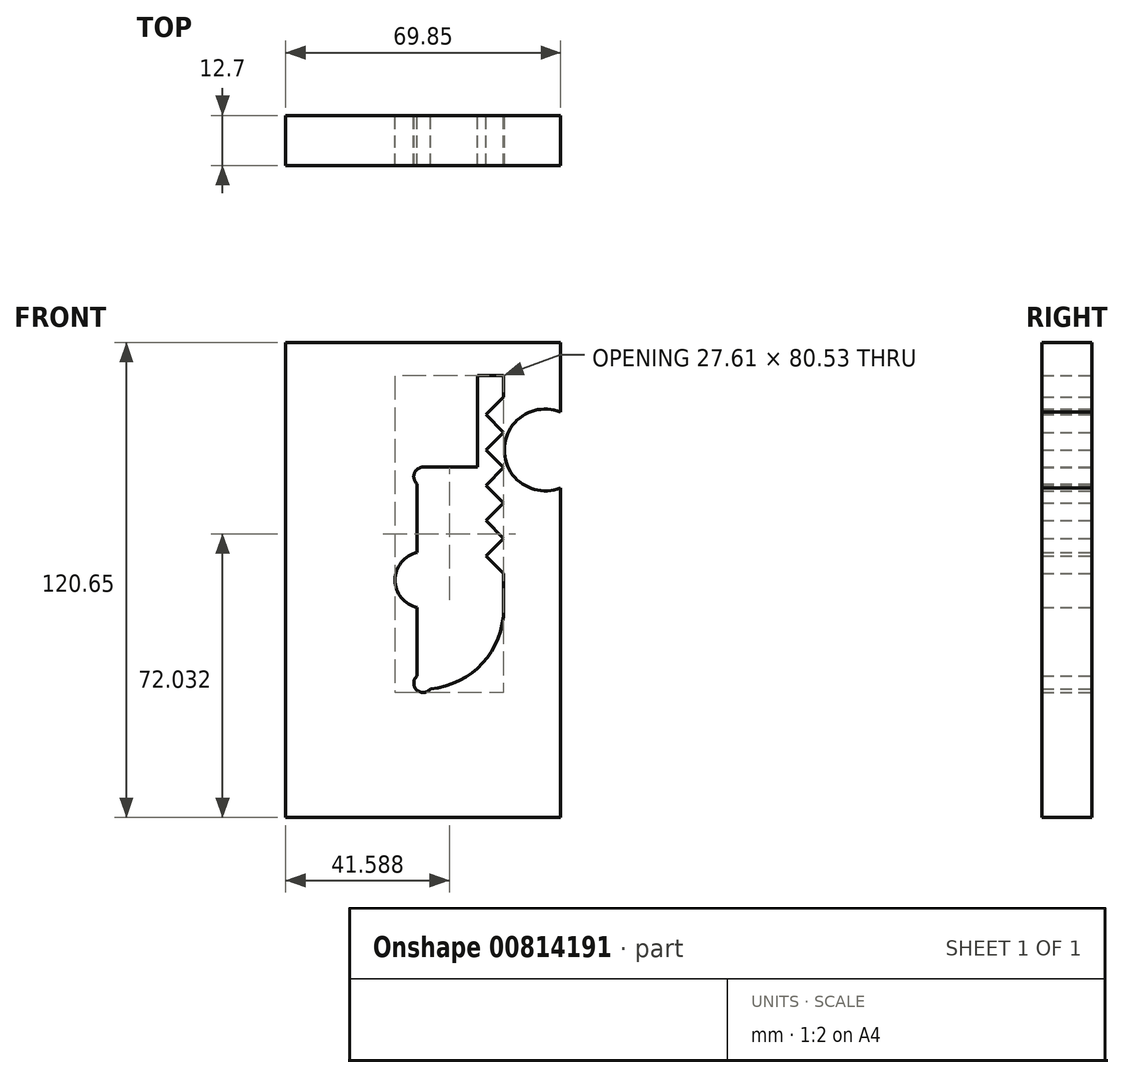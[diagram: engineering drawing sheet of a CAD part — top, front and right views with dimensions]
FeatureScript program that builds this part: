
annotation { "Feature Type Name" : "Feature", "Feature Type Description" : "" }
export const myFeature = defineFeature(function(context is Context, id is Id, definition is map)
    precondition{}
    {
        {
            var Q0;
            Q0=qCreatedBy(makeId("Front.planeOp"),FACE);
            var sketch = newSketch(context, id + "F0", { "sketchPlane" : qUnion([Q0])});
            skLineSegment(sketch, "E0.bottom", {"start": v(-44.77, 47.96) * mm, "end": v(25.08, 47.96) * mm});
            skLineSegment(sketch, "E0.top", {"start": v(-44.77, -72.7) * mm, "end": v(25.08, -72.7) * mm});
            skLineSegment(sketch, "E0.left", {"start": v(-44.77, 47.96) * mm, "end": v(-44.77, -72.7) * mm});
            skLineSegment(sketch, "E0.right", {"start": v(25.08, 47.96) * mm, "end": v(25.08, -72.7) * mm});
            skPoint(sketch, "E0.middle", {"position": v(-9.84, -12.37) * mm});
            skCircle(sketch, "E1", {"center": v(-9.84, -12.37) * mm, "radius": 5.56 * mm});
            skCircle(sketch, "E2", {"center": v(-9.84, -12.37) * mm, "radius": 7.14 * mm});
            skCircle(sketch, "E3", {"center": v(-9.84, -38.55) * mm, "radius": 2.38 * mm});
            skLineSegment(sketch, "E4", {"start": v(-11.36, -19.35) * mm, "end": v(-11.36, -36.7) * mm});
            skLineSegment(sketch, "E5", {"start": v(-8.27, -19.33) * mm, "end": v(-8.27, -36.76) * mm});
            skLineSegment(sketch, "E6", {"start": v(-11.36, -5.38) * mm, "end": v(-11.36, 12.08) * mm});
            skLineSegment(sketch, "E7", {"start": v(-8.33, -5.38) * mm, "end": v(-8.33, 12.1) * mm});
            skCircle(sketch, "E8", {"center": v(-9.86, 13.93) * mm, "radius": 2.38 * mm});
            skPoint(sketch, "E8.third.point", {"position": v(-9.84, 16.31) * mm});
            skLineSegment(sketch, "E9", {"start": v(-9.84, 16.31) * mm, "end": v(3.94, 16.31) * mm});
            skLineSegment(sketch, "E10", {"start": v(3.94, 16.31) * mm, "end": v(3.94, 12.1) * mm});
            skLineSegment(sketch, "E11", {"start": v(3.94, 12.1) * mm, "end": v(-8.33, 12.1) * mm});
            skLineSegment(sketch, "E12", {"start": v(3.94, -19.73) * mm, "end": v(3.94, 16.31) * mm});
            skLineSegment(sketch, "E13", {"start": v(3.94, -19.73) * mm, "end": v(3.94, -19.73) * mm});
            skLineSegment(sketch, "E14", {"start": v(10.62, -19.73) * mm, "end": v(3.94, -19.73) * mm});
            skLineSegment(sketch, "E15", {"start": v(3.94, 16.31) * mm, "end": v(3.94, 39.6) * mm});
            skLineSegment(sketch, "E16", {"start": v(3.94, 39.6) * mm, "end": v(10.62, 39.6) * mm});
            skLineSegment(sketch, "E17", {"start": v(10.62, 39.6) * mm, "end": v(10.62, 34.15) * mm});
            skPoint(sketch, "E18.endSnap0", {"position": v(3.94, -1.7) * mm});
            skArc(sketch, "E19", {"start": v(-7.95, -40) * mm, "mid": v(5.28, -33.48) * mm, "end": v(10.62, -19.73) * mm});
            skArc(sketch, "E20", {"start": v(-8.27, -36.76) * mm, "mid": v(0.57, -30.2) * mm, "end": v(3.94, -19.73) * mm});
            skLineSegment(sketch, "E21", {"start": v(10.62, 34.15) * mm, "end": v(6.13, 29.66) * mm});
            skLineSegment(sketch, "E22", {"start": v(6.13, 29.66) * mm, "end": v(10.62, 25.17) * mm});
            skLineSegment(sketch, "E23", {"start": v(10.62, 25.17) * mm, "end": v(6.14, 20.68) * mm});
            skLineSegment(sketch, "E24", {"start": v(6.14, 20.68) * mm, "end": v(10.62, 16.2) * mm});
            skLineSegment(sketch, "E25", {"start": v(10.62, 16.2) * mm, "end": v(6.14, 11.7) * mm});
            skLineSegment(sketch, "E26", {"start": v(6.14, 11.7) * mm, "end": v(10.62, 7.22) * mm});
            skLineSegment(sketch, "E27", {"start": v(10.62, 7.22) * mm, "end": v(6.13, 2.73) * mm});
            skLineSegment(sketch, "E28", {"start": v(6.13, 2.73) * mm, "end": v(10.62, -1.76) * mm});
            skLineSegment(sketch, "E29", {"start": v(10.62, -1.76) * mm, "end": v(6.13, -6.25) * mm});
            skLineSegment(sketch, "E30", {"start": v(6.13, -6.25) * mm, "end": v(10.62, -10.74) * mm});
            skLineSegment(sketch, "E31", {"start": v(10.62, -10.74) * mm, "end": v(10.62, -19.73) * mm});
            skCircle(sketch, "E32", {"center": v(21.15, 20.68) * mm, "radius": 10.39 * mm});
            skPoint(sketch, "E32.centerSnap0", {"position": v(10.62, 20.68) * mm});
            skCircle(sketch, "E33", {"center": v(21.15, 20.68) * mm, "radius": 3.18 * mm});
            skCircle(sketch, "E34", {"center": v(27.15, 15.63) * mm, "radius": 0.6 * mm});
            skSolve(sketch);
        }
        {
            var Q0;
            {var subQ0=sQuery(id+"F0.wireOp",EDGE,"E32");var subQ1=sQuery(id+"F0.wireOp",EDGE,"E0.right");var subQ2=makeQuery(id+"F0.imprint","INTERSECT",VERTEX,{"disambiguationData":[OD(0.0)],"derivedFrom":[subQ1,subQ0]});Q0=makeQuery(id+"F0.imprint","IMPRINT",FACE,{"disambiguationData":[TD([[makeQuery(id+"F0.imprint","IMPRINT",EDGE,{"disambiguationData":[TD([[subQ2,-1.0]])],"derivedFrom":subQ1}),1.0]])]});}
            var Q1;
            {var subQ0=sQuery(id+"F0.wireOp",EDGE,"E32");var subQ1=sQuery(id+"F0.wireOp",EDGE,"E0.right");var subQ2=makeQuery(id+"F0.imprint","INTERSECT",VERTEX,{"disambiguationData":[OD(0.0)],"derivedFrom":[subQ1,subQ0]});Q1=makeQuery(id+"F0.imprint","IMPRINT",FACE,{"disambiguationData":[TD([[makeQuery(id+"F0.imprint","IMPRINT",EDGE,{"disambiguationData":[TD([[subQ2,-1.0]])],"derivedFrom":subQ1}),-1.0]])]});}
            extrude(context, id + "F1", {"entities" : qUnion([Q0, Q1]), "depth" : 12.7 * mm, "offsetDistance" : 25.4 * mm});
        }
    });
